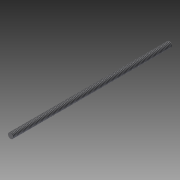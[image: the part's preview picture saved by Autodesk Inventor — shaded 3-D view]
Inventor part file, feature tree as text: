
AUTODESK INVENTOR PART (.ipt)
format: ipt  version: 2014 SP1 (Build 180222100, 222)  size: 69,632 bytes
history: native  units: in
note: dims shown in document units (in); Inventor stores cm internally (conversion verified against a paired STEP export)
features: extrude x1, thread x1, sketch x1
ambient origin geometry x8: Origin, YZ Plane, XZ Plane, XY Plane, X Axis, Y Axis, Z Axis, Center Point
bodies: Solid1 (feature_tree)
feature tree (3):
  extrude  "Extrusion1"  Depth=5.5in TaperAngle=0.0deg
  thread  "Thread1"  [1 undecoded]
  sketch  "Sketch1"  dims[d0=0.185in d1=5.5in d2=0.0in d3=1.0in d4=0.0in]
note: 1 required parameter value undecoded (feature->parameter linkage not recoverable at this tier; creation-order binding heuristic only, values carry confidence <= 0.55)
